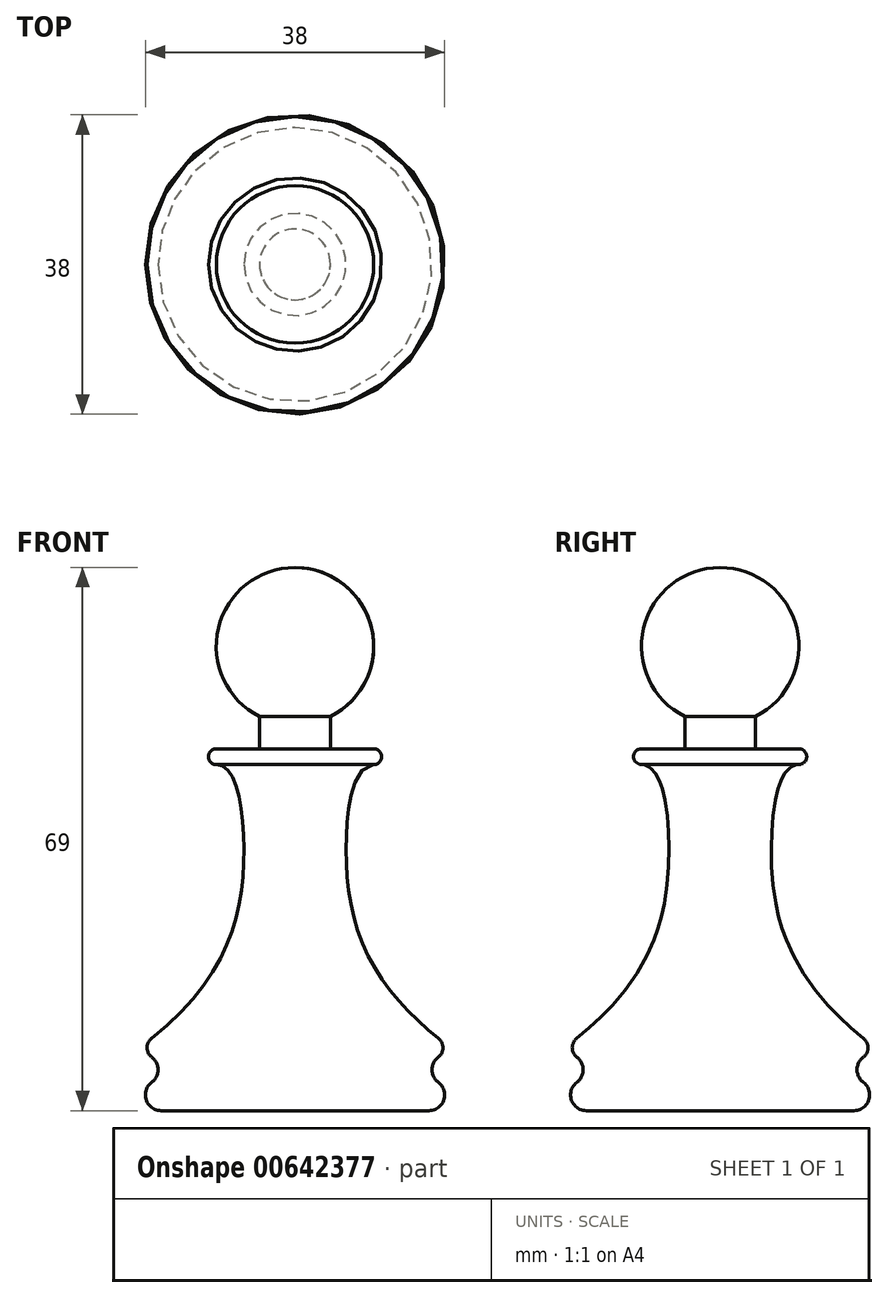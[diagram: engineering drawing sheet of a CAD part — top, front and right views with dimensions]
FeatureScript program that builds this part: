
annotation { "Feature Type Name" : "Feature", "Feature Type Description" : "" }
export const myFeature = defineFeature(function(context is Context, id is Id, definition is map)
    precondition{}
    {
        {
            var Q0;
            Q0=qCreatedBy(makeId("Front.planeOp"),FACE);
            var sketch = newSketch(context, id + "F0", { "sketchPlane" : qUnion([Q0])});
            skLineSegment(sketch, "E0", {"start": v(0, 0) * mm, "end": v(0, 69) * mm});
            skLineSegment(sketch, "E1", {"start": v(0, 0) * mm, "end": v(17, 0) * mm});
            skArc(sketch, "E2", {"start": v(17, 0) * mm, "mid": v(18.9, 1.37) * mm, "end": v(18.2, 3.6) * mm});
            skArc(sketch, "E3", {"start": v(18.2, 6.8) * mm, "mid": v(18.79, 7.98) * mm, "end": v(18.23, 9.17) * mm});
            skFitSpline(sketch, "E4", {"points": [v(10, 43.97) * mm, v(6.5, 33) * mm, v(18.23, 9.17) * mm], "startDerivative": vector(-20.14, 0) * mm, "endDerivative": vector(48.4, -38.68) * mm});
            skPoint(sketch, "E5", {"position": v(8.5, 0) * mm});
            skLineSegment(sketch, "E6", {"start": v(10, 45.97) * mm, "end": v(4.5, 45.97) * mm});
            skLineSegment(sketch, "E7", {"start": v(4.5, 45.97) * mm, "end": v(4.5, 50.07) * mm});
            skArc(sketch, "E8", {"start": v(4.5, 50.07) * mm, "mid": v(9.73, 61.31) * mm, "end": v(0, 69) * mm});
            skLineSegment(sketch, "E9", {"start": v(10, 45.97) * mm, "end": v(10, 44.97) * mm, "construction": true});
            skLineSegment(sketch, "E10", {"start": v(10, 44.97) * mm, "end": v(10, 43.97) * mm, "construction": true});
            skArc(sketch, "E11", {"start": v(10, 43.97) * mm, "mid": v(11, 44.97) * mm, "end": v(10, 45.97) * mm});
            skPoint(sketch, "E12.newPointB", {"position": v(17, 4) * mm});
            skArc(sketch, "E12.filletArc", {"start": v(18.2, 6.8) * mm, "mid": v(17.4, 5.2) * mm, "end": v(18.2, 3.6) * mm});
            skSolve(sketch);
        }
        {
            var Q0;
            Q0=makeQuery(id+"F0.imprint","IMPRINT",FACE,{"disambiguationData":[TD([[makeQuery(id+"F0.imprint","IMPRINT",EDGE,{"derivedFrom":sQuery(id+"F0.wireOp",EDGE,"E0")}),-1.0]])]});
            var Q1;
            Q1=sQuery(id+"F0.wireOp",EDGE,"E0");
            revolve(context, id + "F1", {"entities" : qUnion([Q0]), "axis" : qUnion([Q1]), "revolveType" : RevolveType.FULL});
        }
    });
